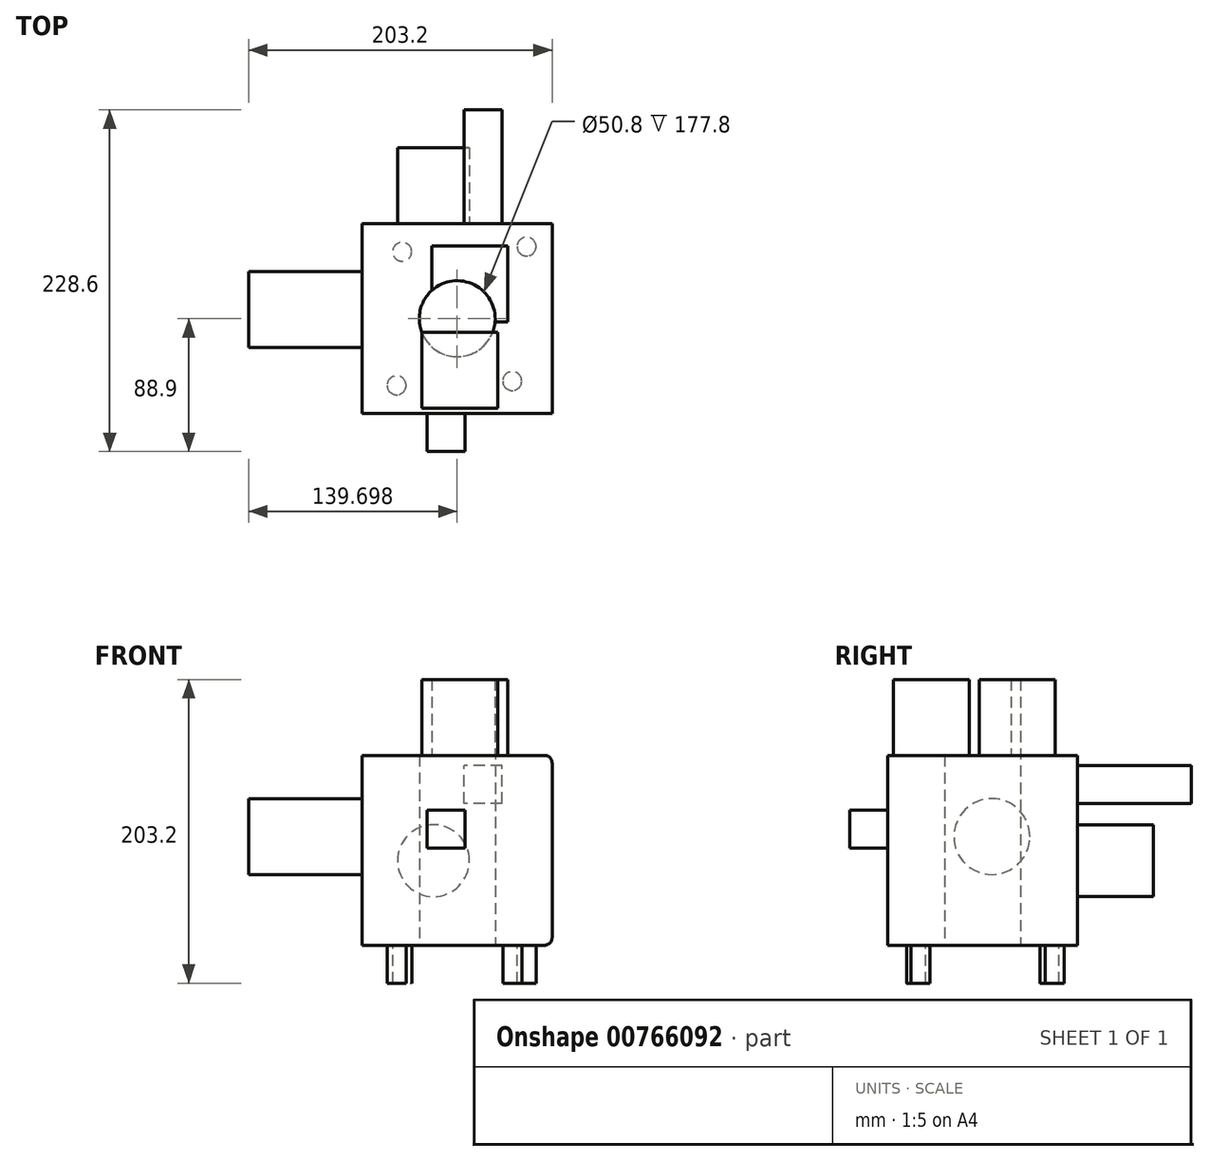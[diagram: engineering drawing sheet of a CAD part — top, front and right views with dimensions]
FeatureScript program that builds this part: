
annotation { "Feature Type Name" : "Feature", "Feature Type Description" : "" }
export const myFeature = defineFeature(function(context is Context, id is Id, definition is map)
    precondition{}
    {
        {
            var Q0;
            Q0=qCreatedBy(makeId("Front.planeOp"),FACE);
            var sketch = newSketch(context, id + "F0", { "sketchPlane" : qUnion([Q0])});
            skLineSegment(sketch, "E0.bottom", {"start": v(-46.14, -14.01) * mm, "end": v(80.86, -14.01) * mm});
            skLineSegment(sketch, "E0.top", {"start": v(-46.14, 112.99) * mm, "end": v(80.86, 112.99) * mm});
            skLineSegment(sketch, "E0.left", {"start": v(-46.14, -14.01) * mm, "end": v(-46.14, 112.99) * mm});
            skLineSegment(sketch, "E0.right", {"start": v(80.86, -14.01) * mm, "end": v(80.86, 112.99) * mm});
            skSolve(sketch);
        }
        {
            var Q0;
            Q0 = qSketchRegion(id + "F0", true);
            extrude(context, id + "F1", {"entities" : qUnion([Q0]), "depth" : 127 * mm, "offsetDistance" : 25.4 * mm});
        }
        {
            var Q0;
            Q0=makeQuery(id+"F1.opExtrude","SWEPT_FACE",FACE,{"disambiguationData":[OSD([sQuery(id+"F0.wireOp",EDGE,"E0.top")])]});
            var sketch = newSketch(context, id + "F2", { "sketchPlane" : qUnion([Q0])});
            skLineSegment(sketch, "E1.bottom", {"start": v(0.48, -65.74) * mm, "end": v(51.28, -65.74) * mm});
            skLineSegment(sketch, "E1.top", {"start": v(0.48, -14.94) * mm, "end": v(51.28, -14.94) * mm});
            skLineSegment(sketch, "E1.left", {"start": v(0.48, -65.74) * mm, "end": v(0.48, -14.94) * mm});
            skLineSegment(sketch, "E1.right", {"start": v(51.28, -65.74) * mm, "end": v(51.28, -14.94) * mm});
            skSolve(sketch);
        }
        {
            var Q0;
            Q0 = qSketchRegion(id + "F2", true);
            extrude(context, id + "F3", {"entities" : qUnion([Q0]), "operationType" : NewBodyOperationType.ADD, "depth" : 50.8 * mm, "offsetDistance" : 25.4 * mm});
        }
        {
            var Q0;
            Q0=makeQuery(id+"F1.opExtrude","SWEPT_FACE",FACE,{"disambiguationData":[OSD([sQuery(id+"F0.wireOp",EDGE,"E0.left")])]});
            var sketch = newSketch(context, id + "F4", { "sketchPlane" : qUnion([Q0])});
            skCircle(sketch, "E2", {"center": v(57.33, 58.66) * mm, "radius": 25.4 * mm});
            skSolve(sketch);
        }
        {
            var Q0;
            Q0 = qSketchRegion(id + "F4", true);
            extrude(context, id + "F5", {"entities" : qUnion([Q0]), "operationType" : NewBodyOperationType.ADD, "depth" : 76.2 * mm, "offsetDistance" : 25.4 * mm});
        }
        {
            var Q0;
            Q0=makeQuery(id+"F1.opExtrude","CAP_FACE",FACE,{"disambiguationData":[OSD([sQuery(id+"F0.wireOp",EDGE,"E0.bottom"),sQuery(id+"F0.wireOp",EDGE,"E0.top"),sQuery(id+"F0.wireOp",EDGE,"E0.left"),sQuery(id+"F0.wireOp",EDGE,"E0.right")])],"isStart":true});
            var sketch = newSketch(context, id + "F6", { "sketchPlane" : qUnion([Q0])});
            skCircle(sketch, "E3", {"center": v(-1.43, 42.58) * mm, "radius": 24.03 * mm});
            skPoint(sketch, "E3.first.point", {"position": v(-22.96, 53.24) * mm});
            skPoint(sketch, "E3.second.point", {"position": v(17.04, 27.22) * mm});
            skPoint(sketch, "E3.third.point", {"position": v(4.55, 65.85) * mm});
            skSolve(sketch);
        }
        {
            var Q0;
            Q0 = qSketchRegion(id + "F6", true);
            extrude(context, id + "F7", {"entities" : qUnion([Q0]), "operationType" : NewBodyOperationType.ADD, "depth" : 50.8 * mm, "offsetDistance" : 25.4 * mm});
        }
        {
            var Q0;
            Q0=makeQuery(id+"F1.opExtrude","CAP_FACE",FACE,{"disambiguationData":[OSD([sQuery(id+"F0.wireOp",EDGE,"E0.bottom"),sQuery(id+"F0.wireOp",EDGE,"E0.top"),sQuery(id+"F0.wireOp",EDGE,"E0.left"),sQuery(id+"F0.wireOp",EDGE,"E0.right")])],"isStart":true});
            var sketch = newSketch(context, id + "F8", { "sketchPlane" : qUnion([Q0])});
            skLineSegment(sketch, "E4.bottom", {"start": v(-47.33, 80.86) * mm, "end": v(-21.93, 80.86) * mm});
            skLineSegment(sketch, "E4.top", {"start": v(-47.33, 106.26) * mm, "end": v(-21.93, 106.26) * mm});
            skLineSegment(sketch, "E4.left", {"start": v(-47.33, 80.86) * mm, "end": v(-47.33, 106.26) * mm});
            skLineSegment(sketch, "E4.right", {"start": v(-21.93, 80.86) * mm, "end": v(-21.93, 106.26) * mm});
            skSolve(sketch);
        }
        {
            var Q0;
            Q0 = qSketchRegion(id + "F8", true);
            extrude(context, id + "F9", {"entities" : qUnion([Q0]), "operationType" : NewBodyOperationType.ADD, "depth" : 76.2 * mm, "offsetDistance" : 25.4 * mm});
        }
        {
            var Q0;
            Q0=makeQuery(id+"F1.opExtrude","SWEPT_FACE",FACE,{"disambiguationData":[OSD([sQuery(id+"F0.wireOp",EDGE,"E0.bottom")])]});
            var sketch = newSketch(context, id + "F10", { "sketchPlane" : qUnion([Q0])});
            skPoint(sketch, "E5", {"position": v(17.36, 63.5) * mm});
            skPoint(sketch, "E5.positionSnap0", {"position": v(17.36, 0) * mm});
            skPoint(sketch, "E5.positionSnap1", {"position": v(80.86, 63.5) * mm});
            skSolve(sketch);
        }
        {
            var Q0;
            Q0=sQuery(id+"F10.wireOp",VERTEX,"E5");
            var Q1;
            Q1=makeQuery(id+"F1.opExtrude","SWEPT_BODY",BODY,{"disambiguationData":[OSD([sQuery(id+"F0.wireOp",EDGE,"E0.bottom"),sQuery(id+"F0.wireOp",EDGE,"E0.top"),sQuery(id+"F0.wireOp",EDGE,"E0.left"),sQuery(id+"F0.wireOp",EDGE,"E0.right")])]});
            hole(context, id + "F11", {"style" : HoleStyle.SIMPLE, "endStyle" : HoleEndStyle.THROUGH, "holeDiameter" : 50.8 * mm, "majorDiameter" : 6.35 * mm, "isTappedThrough" : true, "tappedDepth" : 12.7 * mm, "tapClearance" : 3, "locations" : qUnion([Q0]), "scope" : qUnion([Q1])});
        }
        {
            var Q0;
            Q0=makeQuery(id+"F1.opExtrude","SWEPT_EDGE",EDGE,{"disambiguationData":[OSD([sQuery(id+"F0.wireOp",EDGE,"E0.bottom"),sQuery(id+"F0.wireOp",EDGE,"E0.right")])]});
            var Q1;
            Q1=makeQuery(id+"F1.opExtrude","SWEPT_EDGE",EDGE,{"disambiguationData":[OSD([sQuery(id+"F0.wireOp",EDGE,"E0.top"),sQuery(id+"F0.wireOp",EDGE,"E0.right")])]});
            fillet(context, id + "F12", {"entities" : qUnion([Q0, Q1]), "radius" : 5.08 * mm, "tangentPropagation" : true, "allowEdgeOverflow" : false});
        }
        {
            var Q0;
            Q0=makeQuery(id+"F1.opExtrude","CAP_FACE",FACE,{"disambiguationData":[OSD([sQuery(id+"F0.wireOp",EDGE,"E0.bottom"),sQuery(id+"F0.wireOp",EDGE,"E0.top"),sQuery(id+"F0.wireOp",EDGE,"E0.left"),sQuery(id+"F0.wireOp",EDGE,"E0.right")])],"isStart":false});
            var sketch = newSketch(context, id + "F13", { "sketchPlane" : qUnion([Q0])});
            skLineSegment(sketch, "E6.bottom", {"start": v(-2.69, 50.99) * mm, "end": v(22.71, 50.99) * mm});
            skLineSegment(sketch, "E6.top", {"start": v(-2.69, 76.39) * mm, "end": v(22.71, 76.39) * mm});
            skLineSegment(sketch, "E6.left", {"start": v(-2.69, 50.99) * mm, "end": v(-2.69, 76.39) * mm});
            skLineSegment(sketch, "E6.right", {"start": v(22.71, 50.99) * mm, "end": v(22.71, 76.39) * mm});
            skSolve(sketch);
        }
        {
            var Q0;
            Q0=makeQuery(id+"F13.imprint","IMPRINT",FACE,{"disambiguationData":[TD([[makeQuery(id+"F13.imprint","IMPRINT",EDGE,{"derivedFrom":sQuery(id+"F13.wireOp",EDGE,"E6.bottom")}),1.0]])]});
            extrude(context, id + "F14", {"entities" : qUnion([Q0]), "operationType" : NewBodyOperationType.ADD, "depth" : 25.4 * mm, "offsetDistance" : 25.4 * mm});
        }
        {
            var Q0;
            Q0=makeQuery(id+"F1.opExtrude","SWEPT_FACE",FACE,{"disambiguationData":[OSD([sQuery(id+"F0.wireOp",EDGE,"E0.bottom")])]});
            var sketch = newSketch(context, id + "F15", { "sketchPlane" : qUnion([Q0])});
            skCircle(sketch, "E7", {"center": v(-19.48, 18.7) * mm, "radius": 6.35 * mm});
            skSolve(sketch);
        }
        {
            var Q0;
            Q0=makeQuery(id+"F15.imprint","IMPRINT",FACE,{"disambiguationData":[TD([[makeQuery(id+"F15.imprint","IMPRINT",EDGE,{"derivedFrom":sQuery(id+"F15.wireOp",EDGE,"E7")}),1.0]])]});
            var sketch = newSketch(context, id + "F16", { "sketchPlane" : qUnion([Q0])});
            skSolve(sketch);
        }
        {
            var Q0;
            Q0 = qSketchRegion(id + "F16", true);
            var Q1;
            Q1=makeQuery(id+"F15.imprint","IMPRINT",FACE,{"disambiguationData":[TD([[makeQuery(id+"F15.imprint","IMPRINT",EDGE,{"derivedFrom":sQuery(id+"F15.wireOp",EDGE,"E7")}),1.0]])]});
            extrude(context, id + "F17", {"entities" : qUnion([Q0, Q1]), "operationType" : NewBodyOperationType.ADD, "depth" : 25.4 * mm, "offsetDistance" : 25.4 * mm});
        }
        {
            var Q0;
            Q0=makeQuery(id+"F1.opExtrude","SWEPT_FACE",FACE,{"disambiguationData":[OSD([sQuery(id+"F0.wireOp",EDGE,"E0.bottom")])]});
            var sketch = newSketch(context, id + "F18", { "sketchPlane" : qUnion([Q0])});
            skCircle(sketch, "E8", {"center": v(54.19, 105.27) * mm, "radius": 6.35 * mm});
            skSolve(sketch);
        }
        {
            var Q0;
            Q0 = qSketchRegion(id + "F18", true);
            extrude(context, id + "F19", {"entities" : qUnion([Q0]), "operationType" : NewBodyOperationType.ADD, "depth" : 25.4 * mm, "offsetDistance" : 25.4 * mm});
        }
        {
            var Q0;
            Q0=makeQuery(id+"F1.opExtrude","SWEPT_FACE",FACE,{"disambiguationData":[OSD([sQuery(id+"F0.wireOp",EDGE,"E0.bottom")])]});
            var sketch = newSketch(context, id + "F20", { "sketchPlane" : qUnion([Q0])});
            skCircle(sketch, "E9", {"center": v(-23.16, 108.12) * mm, "radius": 6.35 * mm});
            skSolve(sketch);
        }
        {
            var Q0;
            Q0 = qSketchRegion(id + "F20", true);
            extrude(context, id + "F21", {"entities" : qUnion([Q0]), "operationType" : NewBodyOperationType.ADD, "depth" : 25.4 * mm, "offsetDistance" : 25.4 * mm});
        }
        {
            var Q0;
            Q0=makeQuery(id+"F1.opExtrude","SWEPT_FACE",FACE,{"disambiguationData":[OSD([sQuery(id+"F0.wireOp",EDGE,"E0.bottom")])]});
            var sketch = newSketch(context, id + "F22", { "sketchPlane" : qUnion([Q0])});
            skCircle(sketch, "E10", {"center": v(63.83, 15.25) * mm, "radius": 6.35 * mm});
            skSolve(sketch);
        }
        {
            var Q0;
            Q0 = qSketchRegion(id + "F22", true);
            extrude(context, id + "F23", {"entities" : qUnion([Q0]), "operationType" : NewBodyOperationType.ADD, "depth" : 25.4 * mm, "offsetDistance" : 25.4 * mm});
        }
        {
            var Q0;
            Q0=makeQuery(id+"F1.opExtrude","SWEPT_FACE",FACE,{"disambiguationData":[OSD([sQuery(id+"F0.wireOp",EDGE,"E0.top")])]});
            var sketch = newSketch(context, id + "F24", { "sketchPlane" : qUnion([Q0])});
            skLineSegment(sketch, "E11.bottom", {"start": v(44.44, -123.4) * mm, "end": v(-6.36, -123.4) * mm});
            skLineSegment(sketch, "E11.top", {"start": v(44.44, -72.6) * mm, "end": v(-6.36, -72.6) * mm});
            skLineSegment(sketch, "E11.left", {"start": v(44.44, -123.4) * mm, "end": v(44.44, -72.6) * mm});
            skLineSegment(sketch, "E11.right", {"start": v(-6.36, -123.4) * mm, "end": v(-6.36, -72.6) * mm});
            skSolve(sketch);
        }
        {
            var Q0;
            Q0 = qSketchRegion(id + "F24", true);
            extrude(context, id + "F25", {"entities" : qUnion([Q0]), "operationType" : NewBodyOperationType.ADD, "depth" : 50.8 * mm, "offsetDistance" : 25.4 * mm});
        }
    });
